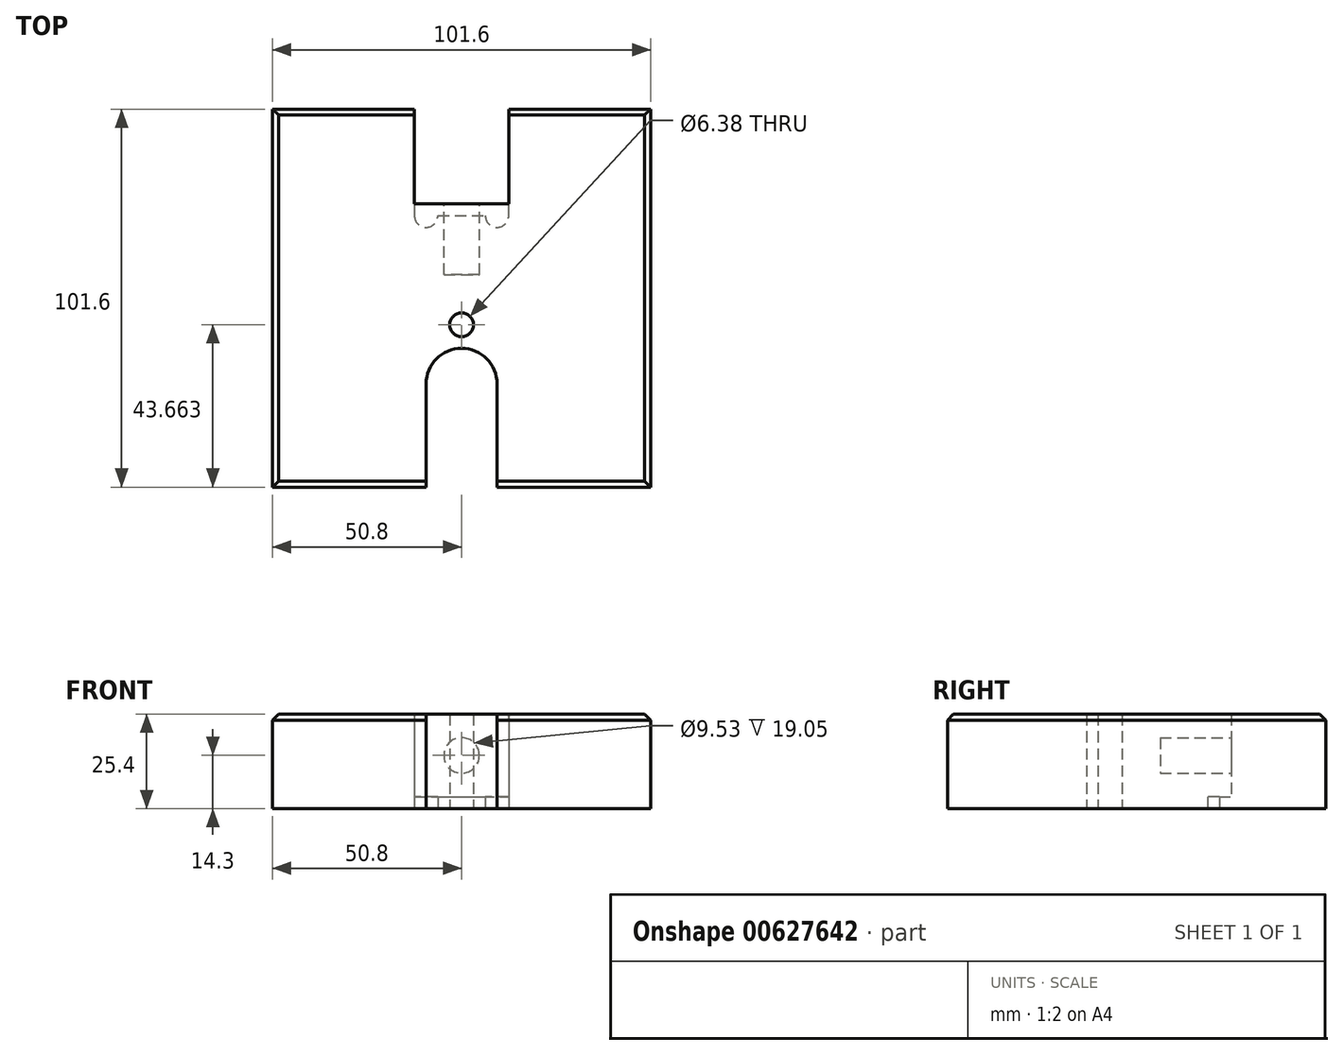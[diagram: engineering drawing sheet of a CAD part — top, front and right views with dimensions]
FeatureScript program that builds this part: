
annotation { "Feature Type Name" : "Feature", "Feature Type Description" : "" }
export const myFeature = defineFeature(function(context is Context, id is Id, definition is map)
    precondition{}
    {
        {
            var Q0;
            Q0=qCreatedBy(makeId("Top.planeOp"),FACE);
            var sketch = newSketch(context, id + "F0", { "sketchPlane" : qUnion([Q0])});
            skLineSegment(sketch, "E0.bottom", {"start": v(-50.8, 50.8) * mm, "end": v(-12.7, 50.8) * mm});
            skLineSegment(sketch, "E0.top", {"start": v(-50.8, -50.8) * mm, "end": v(-9.53, -50.8) * mm});
            skLineSegment(sketch, "E0.left", {"start": v(-50.8, 50.8) * mm, "end": v(-50.8, -50.8) * mm});
            skLineSegment(sketch, "E0.right", {"start": v(50.8, 50.8) * mm, "end": v(50.8, -50.8) * mm});
            skPoint(sketch, "E0.middle", {"position": v(0, 0) * mm});
            skLineSegment(sketch, "E1", {"start": v(-9.53, -50.8) * mm, "end": v(-9.53, -23.01) * mm});
            skLineSegment(sketch, "E2", {"start": v(9.53, -23.01) * mm, "end": v(9.53, -50.8) * mm});
            skArc(sketch, "E3", {"start": v(9.53, -23.01) * mm, "mid": v(0, -13.49) * mm, "end": v(-9.53, -23.01) * mm});
            skLineSegment(sketch, "E4.trimOffspring", {"start": v(9.53, -50.8) * mm, "end": v(50.8, -50.8) * mm});
            skLineSegment(sketch, "E5", {"start": v(-12.7, 50.8) * mm, "end": v(-12.7, 25.4) * mm});
            skLineSegment(sketch, "E6", {"start": v(-12.7, 25.4) * mm, "end": v(12.7, 25.4) * mm});
            skLineSegment(sketch, "E7", {"start": v(12.7, 25.4) * mm, "end": v(12.7, 50.8) * mm});
            skLineSegment(sketch, "E8.trimOffspring", {"start": v(12.7, 50.8) * mm, "end": v(50.8, 50.8) * mm});
            skCircle(sketch, "E9", {"center": v(0, -7.14) * mm, "radius": 3.19 * mm});
            skSolve(sketch);
        }
        {
            var Q0;
            Q0 = qSketchRegion(id + "F0", true);
            extrude(context, id + "F1", {"entities" : qUnion([Q0]), "depth" : 25.4 * mm, "offsetDistance" : 25.4 * mm});
        }
        {
            var Q0;
            Q0=makeQuery(id+"F1.opExtrude","CAP_FACE",FACE,{"disambiguationData":[OSD([sQuery(id+"F0.wireOp",EDGE,"E0.bottom"),sQuery(id+"F0.wireOp",EDGE,"E0.top"),sQuery(id+"F0.wireOp",EDGE,"E0.left"),sQuery(id+"F0.wireOp",EDGE,"E0.right"),sQuery(id+"F0.wireOp",EDGE,"E1"),sQuery(id+"F0.wireOp",EDGE,"E2"),sQuery(id+"F0.wireOp",EDGE,"E3"),sQuery(id+"F0.wireOp",EDGE,"E4.trimOffspring"),sQuery(id+"F0.wireOp",EDGE,"E5"),sQuery(id+"F0.wireOp",EDGE,"E6"),sQuery(id+"F0.wireOp",EDGE,"E7"),sQuery(id+"F0.wireOp",EDGE,"E8.trimOffspring"),sQuery(id+"F0.wireOp",EDGE,"E9")])],"isStart":true});
            var sketch = newSketch(context, id + "F2", { "sketchPlane" : qUnion([Q0])});
            skLineSegment(sketch, "E10", {"start": v(-12.7, -25.4) * mm, "end": v(-12.7, -22.23) * mm});
            skLineSegment(sketch, "E11", {"start": v(12.7, -22.22) * mm, "end": v(12.7, -25.4) * mm});
            skArc(sketch, "E12", {"start": v(12.7, -22.23) * mm, "mid": v(9.53, -19.05) * mm, "end": v(6.35, -22.23) * mm});
            skArc(sketch, "E13.MirrorC", {"start": v(-12.7, -22.23) * mm, "mid": v(-9.53, -19.05) * mm, "end": v(-6.35, -22.23) * mm});
            skLineSegment(sketch, "E14", {"start": v(-6.35, -22.23) * mm, "end": v(6.35, -22.23) * mm});
            skLineSegment(sketch, "E15", {"start": v(0, 0) * mm, "end": v(0, -38.91) * mm, "construction": true});
            skSolve(sketch);
        }
        {
            var Q0;
            Q0=makeQuery(id+"F2.imprint","IMPRINT",FACE,{"disambiguationData":[TD([[makeQuery(id+"F2.imprint","IMPRINT",EDGE,{"derivedFrom":sQuery(id+"F2.wireOp",EDGE,"E10")}),-1.0]])]});
            extrude(context, id + "F3", {"entities" : qUnion([Q0]), "operationType" : NewBodyOperationType.REMOVE, "oppositeDirection" : true, "depth" : 3.17 * mm, "offsetDistance" : 25.4 * mm});
        }
        {
            var Q0;
            Q0=makeQuery(id+"F1.opExtrude","CAP_EDGE",EDGE,{"disambiguationData":[OSD([sQuery(id+"F0.wireOp",EDGE,"E0.left")])],"isStart":false});
            var Q1;
            Q1=makeQuery(id+"F1.opExtrude","CAP_EDGE",EDGE,{"disambiguationData":[OSD([sQuery(id+"F0.wireOp",EDGE,"E0.top")])],"isStart":false});
            var Q2;
            Q2=makeQuery(id+"F1.opExtrude","CAP_EDGE",EDGE,{"disambiguationData":[OSD([sQuery(id+"F0.wireOp",EDGE,"E4.trimOffspring")])],"isStart":false});
            var Q3;
            Q3=makeQuery(id+"F1.opExtrude","CAP_EDGE",EDGE,{"disambiguationData":[OSD([sQuery(id+"F0.wireOp",EDGE,"E0.right")])],"isStart":false});
            var Q4;
            Q4=makeQuery(id+"F1.opExtrude","CAP_EDGE",EDGE,{"disambiguationData":[OSD([sQuery(id+"F0.wireOp",EDGE,"E8.trimOffspring")])],"isStart":false});
            var Q5;
            Q5=makeQuery(id+"F1.opExtrude","CAP_EDGE",EDGE,{"disambiguationData":[OSD([sQuery(id+"F0.wireOp",EDGE,"E0.bottom")])],"isStart":false});
            chamfer(context, id + "F4", {"entities" : qUnion([Q0, Q1, Q2, Q3, Q4, Q5]), "width" : 1.6 * mm, "tangentPropagation" : true});
        }
        {
            var Q0;
            Q0=makeQuery(id+"F1.opExtrude","SWEPT_FACE",FACE,{"disambiguationData":[OSD([sQuery(id+"F0.wireOp",EDGE,"E6")])]});
            var sketch = newSketch(context, id + "F5", { "sketchPlane" : qUnion([Q0])});
            skCircle(sketch, "E16", {"center": v(0, 14.3) * mm, "radius": 4.76 * mm});
            skSolve(sketch);
        }
        {
            var Q0;
            Q0 = qSketchRegion(id + "F5", true);
            extrude(context, id + "F6", {"entities" : qUnion([Q0]), "operationType" : NewBodyOperationType.REMOVE, "oppositeDirection" : true, "depth" : 19.05 * mm, "offsetDistance" : 25.4 * mm});
        }
    });
